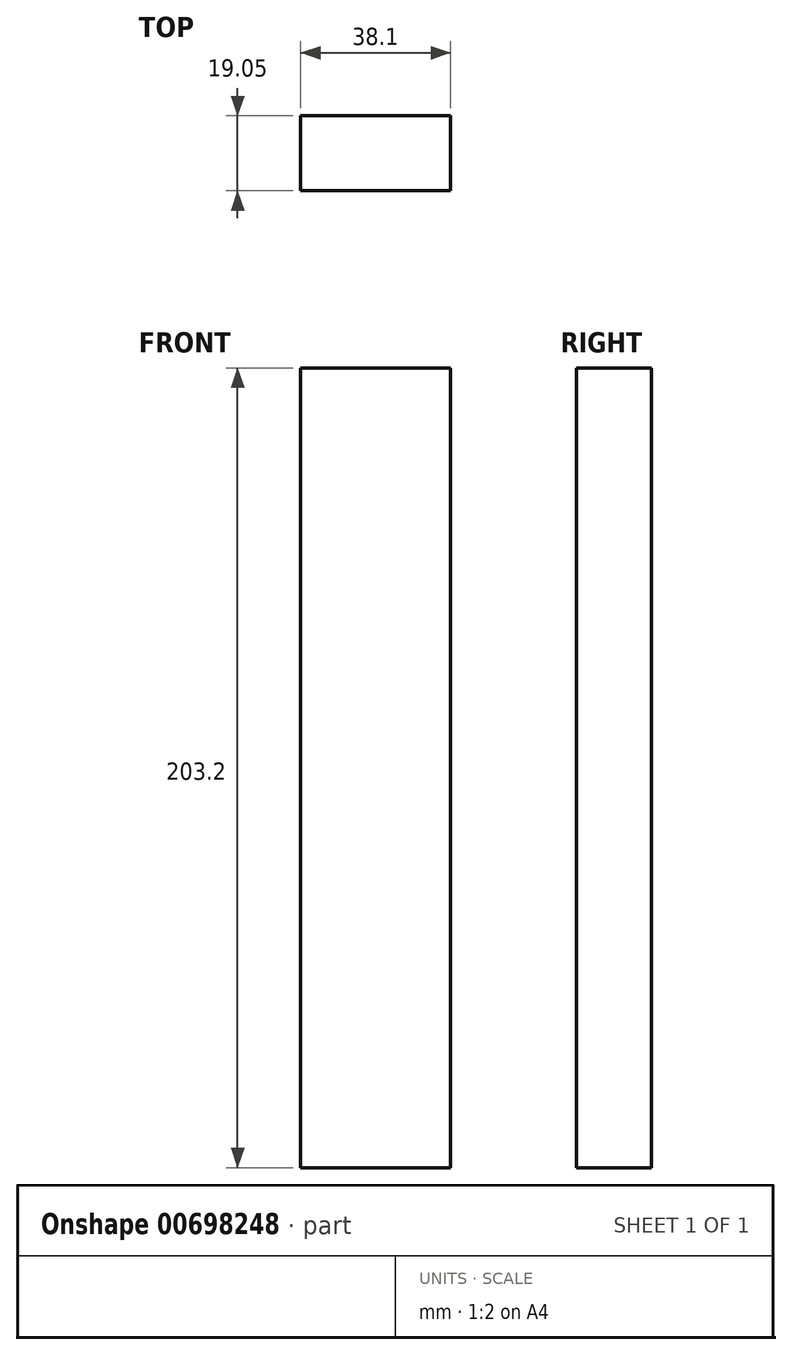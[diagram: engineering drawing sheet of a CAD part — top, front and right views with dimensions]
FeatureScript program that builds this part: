
annotation { "Feature Type Name" : "Feature", "Feature Type Description" : "" }
export const myFeature = defineFeature(function(context is Context, id is Id, definition is map)
    precondition{}
    {
        {
            var Q0;
            Q0=qCreatedBy(makeId("Front.planeOp"),FACE);
            var sketch = newSketch(context, id + "F0", { "sketchPlane" : qUnion([Q0])});
            skLineSegment(sketch, "E0.bottom", {"start": v(-46.66, -148.52) * mm, "end": v(-84.76, -148.52) * mm});
            skLineSegment(sketch, "E0.top", {"start": v(-46.66, 54.68) * mm, "end": v(-84.76, 54.68) * mm});
            skLineSegment(sketch, "E0.left", {"start": v(-46.66, -148.52) * mm, "end": v(-46.66, 54.68) * mm});
            skLineSegment(sketch, "E0.right", {"start": v(-84.76, -148.52) * mm, "end": v(-84.76, 54.68) * mm});
            skSolve(sketch);
        }
        {
            var Q0;
            Q0 = qSketchRegion(id + "F0", true);
            extrude(context, id + "F1", {"entities" : qUnion([Q0]), "depth" : 19.05 * mm, "offsetDistance" : 25.4 * mm});
        }
    });
